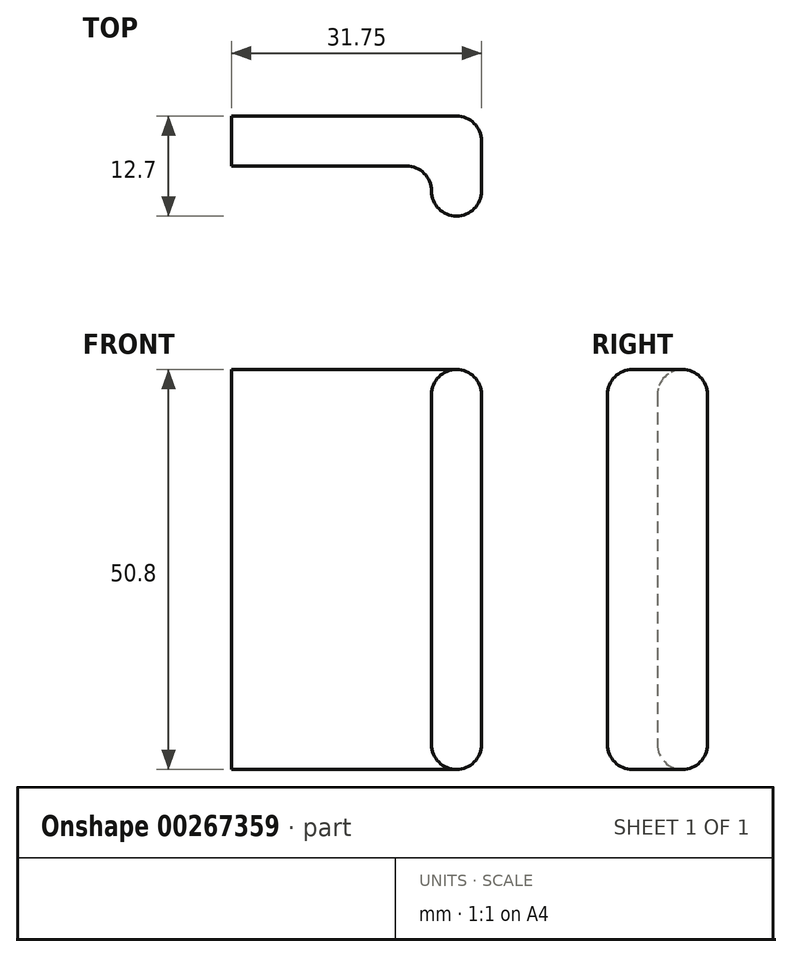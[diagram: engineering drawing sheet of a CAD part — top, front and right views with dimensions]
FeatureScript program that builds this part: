
annotation { "Feature Type Name" : "Feature", "Feature Type Description" : "" }
export const myFeature = defineFeature(function(context is Context, id is Id, definition is map)
    precondition{}
    {
        {
            var Q0;
            Q0=qCreatedBy(makeId("Front.planeOp"),FACE);
            var sketch = newSketch(context, id + "F0", { "sketchPlane" : qUnion([Q0])});
            skLineSegment(sketch, "E0.bottom", {"start": v(-31.75, 50.8) * mm, "end": v(0, 50.8) * mm});
            skLineSegment(sketch, "E0.top", {"start": v(-31.75, 0) * mm, "end": v(0, 0) * mm});
            skLineSegment(sketch, "E0.left", {"start": v(-31.75, 50.8) * mm, "end": v(-31.75, 0) * mm});
            skLineSegment(sketch, "E0.right", {"start": v(0, 50.8) * mm, "end": v(0, 0) * mm});
            skLineSegment(sketch, "E1", {"start": v(-6.35, 50.8) * mm, "end": v(-6.35, 0) * mm});
            skSolve(sketch);
        }
        {
            var Q0;
            Q0 = qSketchRegion(id + "F0", true);
            extrude(context, id + "F1", {"entities" : qUnion([Q0]), "depth" : 6.35 * mm});
        }
        {
            var Q0;
            {var subQ0=sQuery(id+"F0.wireOp",EDGE,"E0.right");Q0=makeQuery(id+"F0.imprint","IMPRINT",FACE,{"disambiguationData":[TD([[makeQuery(id+"F0.imprint","IMPRINT",EDGE,{"derivedFrom":subQ0}),-1.0]])]});}
            extrude(context, id + "F2", {"entities" : qUnion([Q0]), "operationType" : NewBodyOperationType.ADD, "depth" : 12.7 * mm});
        }
        {
            var Q0;
            Q0=makeQuery(id+"F1.opExtrude","CAP_EDGE",EDGE,{"disambiguationData":[OSD([sQuery(id+"F0.wireOp",EDGE,"E0.right")])],"isStart":true});
            var Q1;
            Q1=makeQuery(id+"F2.boolean.opBoolean","INTERSECT",EDGE,{"derivedFrom":[makeQuery(id+"F1.opExtrude","CAP_FACE",FACE,{"disambiguationData":[OSD([sQuery(id+"F0.wireOp",EDGE,"E0.bottom"),sQuery(id+"F0.wireOp",EDGE,"E0.top"),sQuery(id+"F0.wireOp",EDGE,"E0.left"),sQuery(id+"F0.wireOp",EDGE,"E0.right")])],"isStart":false}),makeQuery(id+"F2.opExtrude","SWEPT_FACE",FACE,{"disambiguationData":[OSD([sQuery(id+"F0.wireOp",EDGE,"E1")])]})]});
            var Q2;
            Q2=makeQuery(id+"F2.opExtrude","CAP_FACE",FACE,{"disambiguationData":[OSD([sQuery(id+"F0.wireOp",EDGE,"E0.bottom"),sQuery(id+"F0.wireOp",EDGE,"E0.top"),sQuery(id+"F0.wireOp",EDGE,"E0.right"),sQuery(id+"F0.wireOp",EDGE,"E1")])],"isStart":false});
            fillet(context, id + "F3", {"entities" : qUnion([Q0, Q1, Q2]), "radius" : 3.17 * mm, "tangentPropagation" : true, "allowEdgeOverflow" : false});
        }
        {
            var Q0;
            Q0=makeQuery(id+"F1.opExtrude","CAP_EDGE",EDGE,{"disambiguationData":[OSD([sQuery(id+"F0.wireOp",EDGE,"E0.bottom")])],"isStart":false});
            var Q1;
            Q1=makeQuery(id+"F1.opExtrude","CAP_EDGE",EDGE,{"disambiguationData":[OSD([sQuery(id+"F0.wireOp",EDGE,"E0.top")])],"isStart":false});
            var Q2;
            Q2=makeQuery(id+"F1.opExtrude","CAP_EDGE",EDGE,{"disambiguationData":[OSD([sQuery(id+"F0.wireOp",EDGE,"E0.top")])],"isStart":true});
            var Q3;
            Q3=makeQuery(id+"F1.opExtrude","CAP_EDGE",EDGE,{"disambiguationData":[OSD([sQuery(id+"F0.wireOp",EDGE,"E0.bottom")])],"isStart":true});
            fillet(context, id + "F4", {"entities" : qUnion([Q0, Q1, Q2, Q3]), "radius" : 3.17 * mm, "tangentPropagation" : true, "allowEdgeOverflow" : false});
        }
    });
